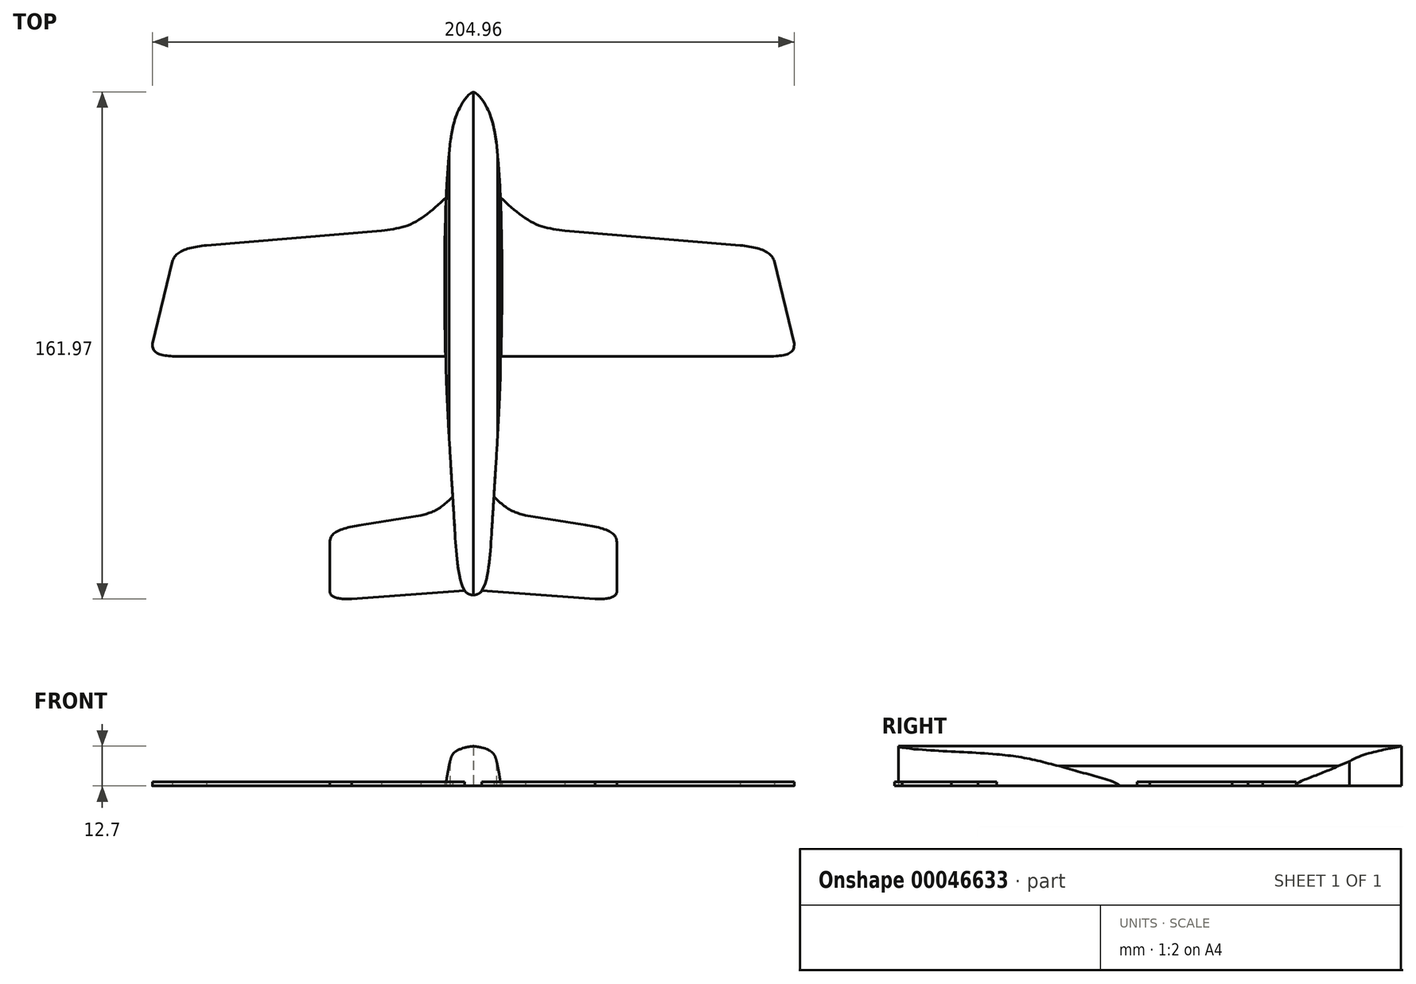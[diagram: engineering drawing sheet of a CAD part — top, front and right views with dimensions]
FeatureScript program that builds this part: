
annotation { "Feature Type Name" : "Feature", "Feature Type Description" : "" }
export const myFeature = defineFeature(function(context is Context, id is Id, definition is map)
    precondition{}
    {
        {
            var Q0;
            Q0=qCreatedBy(makeId("Top.planeOp"),FACE);
            var sketch = newSketch(context, id + "F0", { "sketchPlane" : qUnion([Q0])});
            skLineSegment(sketch, "E0", {"start": v(0, 0) * mm, "end": v(0, -76.2) * mm});
            skLineSegment(sketch, "E1.MirrorCS", {"start": v(0, 0) * mm, "end": v(0, 76.2) * mm});
            skFitSpline(sketch, "E2", {"points": [v(-7.44, 67.81) * mm, v(-8.67, 50.77) * mm, v(-8.86, 0) * mm, v(-6.2, -50.66) * mm, v(-2.73, -74.87) * mm, v(0, -76.2) * mm], "startDerivative": vector(-8.28, -88.5) * mm, "endDerivative": vector(38.3, 0) * mm});
            skFitSpline(sketch, "E3", {"points": [v(-7.44, 67.81) * mm, v(-4.96, 78.16) * mm, v(0, 84.46) * mm], "startDerivative": vector(3.02, 20.87) * mm, "endDerivative": vector(11.67, 4.28) * mm});
            skLineSegment(sketch, "E4", {"start": v(-29.27, 40.16) * mm, "end": v(-85.22, 35.46) * mm});
            skLineSegment(sketch, "E5", {"start": v(-96.13, 30.38) * mm, "end": v(-102.48, 4.1) * mm});
            skLineSegment(sketch, "E6", {"start": v(-92.49, 0) * mm, "end": v(-8.86, 0) * mm});
            skFitSpline(sketch, "E7", {"points": [v(-29.27, 40.16) * mm, v(-19.5, 42.45) * mm, v(-8.67, 50.77) * mm], "startDerivative": vector(21.4, 2.55) * mm, "endDerivative": vector(19.85, 18.28) * mm});
            skFitSpline(sketch, "E8", {"points": [v(-96.87, 27.31) * mm, v(-94.4, 32.86) * mm, v(-79.28, 35.96) * mm], "startDerivative": vector(2.9, 16.19) * mm, "endDerivative": vector(30.2, 2.18) * mm});
            skFitSpline(sketch, "E9", {"points": [v(-101.2, 9.38) * mm, v(-101.92, 1.84) * mm, v(-92, 0) * mm], "startDerivative": vector(-6.2, -19.23) * mm, "endDerivative": vector(23.9, 0) * mm});
            skPoint(sketch, "E10.orphan", {"position": v(-103.47, 0) * mm});
            skLineSegment(sketch, "E11", {"start": v(-16.7, -50.8) * mm, "end": v(-35.05, -53.72) * mm});
            skLineSegment(sketch, "E12", {"start": v(-45.85, -59.35) * mm, "end": v(-45.85, -75.12) * mm});
            skLineSegment(sketch, "E13", {"start": v(-38.88, -77.5) * mm, "end": v(-2.73, -74.87) * mm});
            skFitSpline(sketch, "E14", {"points": [v(-16.7, -50.8) * mm, v(-11.53, -48.88) * mm, v(-6.57, -44.81) * mm], "startDerivative": vector(11.03, 3.05) * mm, "endDerivative": vector(9.25, 8.84) * mm});
            skFitSpline(sketch, "E15", {"points": [v(-45.85, -62.05) * mm, v(-44.9, -56.96) * mm, v(-35.05, -53.72) * mm], "startDerivative": vector(-0.72, 13.7) * mm, "endDerivative": vector(21.08, 3.55) * mm});
            skFitSpline(sketch, "E16", {"points": [v(-45.85, -73.35) * mm, v(-45.1, -76.5) * mm, v(-29.16, -76.8) * mm], "startDerivative": vector(-0.82, -11.62) * mm, "endDerivative": vector(30.27, 2.9) * mm});
            skFitSpline(sketch, "E17.MirrorCS", {"points": [v(7.44, 67.81) * mm, v(8.67, 50.77) * mm, v(8.86, 0) * mm, v(6.2, -50.66) * mm, v(2.73, -74.87) * mm, v(0, -76.2) * mm], "startDerivative": vector(8.28, -88.5) * mm, "endDerivative": vector(-38.3, 0) * mm});
            skFitSpline(sketch, "E18.MirrorCS", {"points": [v(7.44, 67.81) * mm, v(4.96, 78.16) * mm, v(0, 84.46) * mm], "startDerivative": vector(-3.02, 20.87) * mm, "endDerivative": vector(-11.67, 4.28) * mm});
            skLineSegment(sketch, "E19.MirrorCS", {"start": v(29.27, 40.16) * mm, "end": v(85.22, 35.46) * mm});
            skFitSpline(sketch, "E20.MirrorCS", {"points": [v(29.27, 40.16) * mm, v(19.5, 42.45) * mm, v(8.67, 50.77) * mm], "startDerivative": vector(-21.4, 2.55) * mm, "endDerivative": vector(-19.85, 18.28) * mm});
            skLineSegment(sketch, "E21.MirrorCS", {"start": v(96.13, 30.38) * mm, "end": v(102.48, 4.1) * mm});
            skLineSegment(sketch, "E22.MirrorCS", {"start": v(92.49, 0) * mm, "end": v(8.86, 0) * mm});
            skFitSpline(sketch, "E23.MirrorCS", {"points": [v(101.2, 9.38) * mm, v(101.92, 1.84) * mm, v(92, 0) * mm], "startDerivative": vector(6.2, -19.23) * mm, "endDerivative": vector(-23.9, 0) * mm});
            skFitSpline(sketch, "E24.MirrorCS", {"points": [v(96.87, 27.31) * mm, v(94.4, 32.86) * mm, v(79.28, 35.96) * mm], "startDerivative": vector(-2.9, 16.19) * mm, "endDerivative": vector(-30.2, 2.18) * mm});
            skLineSegment(sketch, "E25.MirrorCS", {"start": v(16.7, -50.8) * mm, "end": v(35.05, -53.72) * mm});
            skLineSegment(sketch, "E26.MirrorCS", {"start": v(45.85, -59.35) * mm, "end": v(45.85, -75.12) * mm});
            skLineSegment(sketch, "E27.MirrorCS", {"start": v(38.88, -77.5) * mm, "end": v(2.73, -74.87) * mm});
            skFitSpline(sketch, "E28.MirrorCS", {"points": [v(45.85, -73.35) * mm, v(45.1, -76.5) * mm, v(29.16, -76.8) * mm], "startDerivative": vector(0.82, -11.62) * mm, "endDerivative": vector(-30.27, 2.9) * mm});
            skFitSpline(sketch, "E29.MirrorCS", {"points": [v(45.85, -62.05) * mm, v(44.9, -56.96) * mm, v(35.05, -53.72) * mm], "startDerivative": vector(0.72, 13.7) * mm, "endDerivative": vector(-21.08, 3.55) * mm});
            skFitSpline(sketch, "E30.MirrorCS", {"points": [v(16.7, -50.8) * mm, v(11.53, -48.88) * mm, v(6.57, -44.81) * mm], "startDerivative": vector(-11.03, 3.05) * mm, "endDerivative": vector(-9.25, 8.84) * mm});
            skSolve(sketch);
        }
        {
            var Q0;
            {var subQ11=sQuery(id+"F0.wireOp",EDGE,"E3");Q0=makeQuery(id+"F0.imprint","IMPRINT",FACE,{"disambiguationData":[TD([[makeQuery(id+"F0.imprint","IMPRINT",EDGE,{"derivedFrom":subQ11}),-1.0]])]});}
            extrude(context, id + "F1", {"entities" : qUnion([Q0]), "depth" : 12.7 * mm});
        }
        {
            var Q0;
            Q0=qCreatedBy(makeId("Front.planeOp"),FACE);
            cPlane(context, id + "F2", {"entities" : qUnion([Q0]), "cplaneType" : CPlaneType.OFFSET, "offset" : 88.9 * mm, "width" : 152.4 * mm, "height" : 152.4 * mm});
        }
        {
            var Q0;
            Q0=qCreatedBy(id+"F2.planeOp",FACE);
            var sketch = newSketch(context, id + "F3", { "sketchPlane" : qUnion([Q0])});
            skLineSegment(sketch, "E31", {"start": v(0, 0) * mm, "end": v(0, 12.7) * mm});
            skPoint(sketch, "E32.0.internal.snap0", {"position": v(0, 6.35) * mm});
            skFitSpline(sketch, "E32", {"points": [v(-7.78, 6.35) * mm, v(-6.13, 10.62) * mm, v(0, 12.7) * mm], "startDerivative": vector(3, 12.8) * mm, "endDerivative": vector(13.84, 1.26) * mm});
            skLineSegment(sketch, "E33", {"start": v(-12.93, 16.7) * mm, "end": v(0, 16.7) * mm});
            skFitSpline(sketch, "E34.MirrorCS", {"points": [v(7.78, 6.35) * mm, v(6.13, 10.62) * mm, v(0, 12.7) * mm], "startDerivative": vector(-3, 12.8) * mm, "endDerivative": vector(-13.84, 1.26) * mm});
            skLineSegment(sketch, "E35.MirrorCS", {"start": v(12.93, 6.35) * mm, "end": v(12.93, 16.7) * mm});
            skLineSegment(sketch, "E36.MirrorCS", {"start": v(12.93, 16.7) * mm, "end": v(0, 16.7) * mm});
            skFitSpline(sketch, "E37", {"points": [v(-7.78, 6.35) * mm, v(-8.54, 1.98) * mm, v(-8.7, 0) * mm], "startDerivative": vector(-1.54, -8) * mm, "endDerivative": vector(-0.2, -4.46) * mm});
            skFitSpline(sketch, "E38.MirrorCS", {"points": [v(7.78, 6.35) * mm, v(8.54, 1.98) * mm, v(8.7, 0) * mm], "startDerivative": vector(1.54, -8) * mm, "endDerivative": vector(0.2, -4.46) * mm});
            skLineSegment(sketch, "E39", {"start": v(-12.93, 16.7) * mm, "end": v(-12.93, 0) * mm});
            skLineSegment(sketch, "E40", {"start": v(-12.93, 0) * mm, "end": v(-8.7, 0) * mm});
            skLineSegment(sketch, "E41.MirrorCS", {"start": v(12.93, 0) * mm, "end": v(8.7, 0) * mm});
            skLineSegment(sketch, "E42.MirrorCS", {"start": v(12.93, 16.7) * mm, "end": v(12.93, 0) * mm});
            skSolve(sketch);
        }
        {
            var Q0;
            Q0 = qSketchRegion(id + "F3", true);
            extrude(context, id + "F4", {"entities" : qUnion([Q0]), "operationType" : NewBodyOperationType.REMOVE, "endBound" : BoundingType.THROUGH_ALL, "oppositeDirection" : true, "depth" : 25.4 * mm});
        }
        {
            var Q0;
            {var subQ1=sQuery(id+"F0.wireOp",EDGE,"E7");Q0=makeQuery(id+"F0.imprint","IMPRINT",FACE,{"disambiguationData":[TD([[makeQuery(id+"F0.imprint","IMPRINT",EDGE,{"derivedFrom":subQ1}),-1.0]])]});}
            var Q1;
            {var subQ8=sQuery(id+"F0.wireOp",EDGE,"E20.MirrorCS");Q1=makeQuery(id+"F0.imprint","IMPRINT",FACE,{"disambiguationData":[TD([[makeQuery(id+"F0.imprint","IMPRINT",EDGE,{"derivedFrom":subQ8}),1.0]])]});}
            var Q2;
            {var subQ3=sQuery(id+"F0.wireOp",EDGE,"E25.MirrorCS");Q2=makeQuery(id+"F0.imprint","IMPRINT",FACE,{"disambiguationData":[TD([[makeQuery(id+"F0.imprint","IMPRINT",EDGE,{"derivedFrom":subQ3}),-1.0]])]});}
            var Q3;
            {var subQ9=sQuery(id+"F0.wireOp",EDGE,"E11");Q3=makeQuery(id+"F0.imprint","IMPRINT",FACE,{"disambiguationData":[TD([[makeQuery(id+"F0.imprint","IMPRINT",EDGE,{"derivedFrom":subQ9}),1.0]])]});}
            extrude(context, id + "F5", {"entities" : qUnion([Q0, Q1, Q2, Q3]), "operationType" : NewBodyOperationType.ADD, "depth" : 1.27 * mm});
        }
    });
